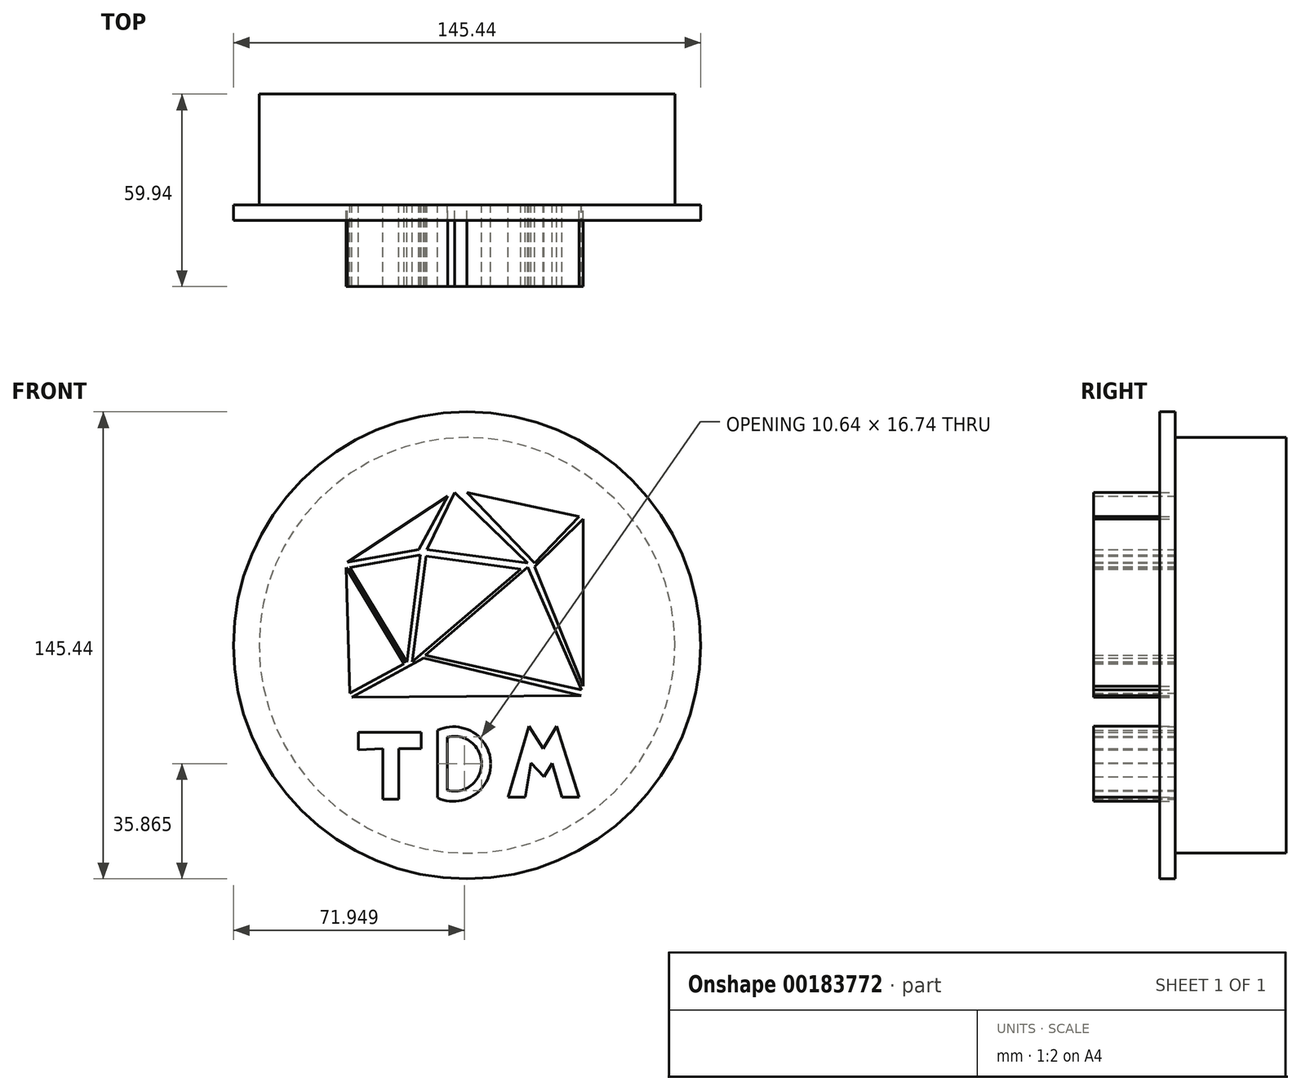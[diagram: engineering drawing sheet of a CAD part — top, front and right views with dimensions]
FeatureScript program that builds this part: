
annotation { "Feature Type Name" : "Feature", "Feature Type Description" : "" }
export const myFeature = defineFeature(function(context is Context, id is Id, definition is map)
    precondition{}
    {
        {
            var Q0;
            Q0=qCreatedBy(makeId("Front.planeOp"),FACE);
            var sketch = newSketch(context, id + "F0", { "sketchPlane" : qUnion([Q0])});
            skLineSegment(sketch, "E0", {"start": v(-26.25, -32.13) * mm, "end": v(-26.25, -47.88) * mm});
            skLineSegment(sketch, "E1", {"start": v(-26.25, -47.88) * mm, "end": v(-21.2, -47.88) * mm});
            skLineSegment(sketch, "E2", {"start": v(-21.2, -47.88) * mm, "end": v(-21.2, -32.13) * mm});
            skLineSegment(sketch, "E3", {"start": v(-21.2, -32.13) * mm, "end": v(-14.28, -32.13) * mm});
            skLineSegment(sketch, "E4", {"start": v(-14.28, -32.13) * mm, "end": v(-14.28, -27.09) * mm});
            skLineSegment(sketch, "E5", {"start": v(-14.28, -27.09) * mm, "end": v(-33.81, -27.09) * mm});
            skLineSegment(sketch, "E6", {"start": v(-33.81, -27.09) * mm, "end": v(-33.81, -32.55) * mm});
            skLineSegment(sketch, "E7", {"start": v(-33.81, -32.55) * mm, "end": v(-26.25, -32.13) * mm});
            skLineSegment(sketch, "E8", {"start": v(-9.24, -26.46) * mm, "end": v(-9.24, -47.46) * mm});
            skArc(sketch, "E9", {"start": v(-9.24, -47.46) * mm, "mid": v(7.38, -36.96) * mm, "end": v(-9.24, -26.46) * mm});
            skLineSegment(sketch, "E10", {"start": v(-6.1, -28.56) * mm, "end": v(-6.1, -45.15) * mm});
            skArc(sketch, "E11", {"start": v(-6.1, -45.15) * mm, "mid": v(4.55, -36.86) * mm, "end": v(-6.1, -28.56) * mm});
            skLineSegment(sketch, "E12", {"start": v(19.32, -25.2) * mm, "end": v(23.73, -32.13) * mm});
            skLineSegment(sketch, "E13", {"start": v(23.73, -32.13) * mm, "end": v(27.93, -25.2) * mm});
            skLineSegment(sketch, "E14", {"start": v(26.46, -36.75) * mm, "end": v(23.94, -40.95) * mm});
            skLineSegment(sketch, "E15", {"start": v(23.94, -40.95) * mm, "end": v(19.95, -36.54) * mm});
            skLineSegment(sketch, "E16", {"start": v(19.95, -36.54) * mm, "end": v(18.06, -47.25) * mm});
            skLineSegment(sketch, "E17", {"start": v(18.06, -47.25) * mm, "end": v(12.81, -47.25) * mm});
            skLineSegment(sketch, "E18", {"start": v(12.81, -47.25) * mm, "end": v(19.32, -25.2) * mm});
            skLineSegment(sketch, "E19", {"start": v(29.6, -47.25) * mm, "end": v(34.86, -47.25) * mm});
            skLineSegment(sketch, "E20", {"start": v(34.86, -47.25) * mm, "end": v(27.93, -25.2) * mm});
            skPoint(sketch, "E21.start.orphan", {"position": v(12.81, -46) * mm});
            skLineSegment(sketch, "E22", {"start": v(29.6, -47.25) * mm, "end": v(26.46, -36.75) * mm});
            skPoint(sketch, "E23.start.orphan", {"position": v(34.86, -45.15) * mm});
            skLineSegment(sketch, "E24", {"start": v(-37.2, 25.82) * mm, "end": v(-5.94, 46.51) * mm});
            skLineSegment(sketch, "E25", {"start": v(-5.94, 46.51) * mm, "end": v(-15.02, 29.84) * mm});
            skLineSegment(sketch, "E26", {"start": v(-15.02, 29.84) * mm, "end": v(-37.2, 25.82) * mm});
            skLineSegment(sketch, "E27", {"start": v(-12.5, 29.84) * mm, "end": v(-3.86, 47.56) * mm});
            skLineSegment(sketch, "E28", {"start": v(-3.86, 47.56) * mm, "end": v(18.92, 25.68) * mm});
            skLineSegment(sketch, "E29", {"start": v(18.92, 25.68) * mm, "end": v(-12.5, 29.84) * mm});
            skLineSegment(sketch, "E30", {"start": v(0, 47.56) * mm, "end": v(21, 25.68) * mm});
            skLineSegment(sketch, "E31", {"start": v(21, 25.68) * mm, "end": v(34.87, 40.1) * mm});
            skLineSegment(sketch, "E32", {"start": v(34.87, 40.1) * mm, "end": v(0, 47.56) * mm});
            skLineSegment(sketch, "E33", {"start": v(36.21, 39.34) * mm, "end": v(36.21, -12.73) * mm});
            skLineSegment(sketch, "E34", {"start": v(-36.49, 24.22) * mm, "end": v(-14.56, 28.2) * mm});
            skLineSegment(sketch, "E35", {"start": v(-14.56, 28.2) * mm, "end": v(-18.74, -5.28) * mm});
            skLineSegment(sketch, "E36", {"start": v(16.68, 23.74) * mm, "end": v(-12.79, 27.76) * mm});
            skLineSegment(sketch, "E37", {"start": v(34.25, -15.6) * mm, "end": v(-35.86, -16.15) * mm});
            skLineSegment(sketch, "E38", {"start": v(-35.86, -16.15) * mm, "end": v(-17.85, -6.35) * mm});
            skPoint(sketch, "E39.start.orphan", {"position": v(-17.85, -7.22) * mm});
            skLineSegment(sketch, "E40", {"start": v(-14.56, 28.2) * mm, "end": v(-36.49, 24.22) * mm});
            skLineSegment(sketch, "E41", {"start": v(-36.49, 24.22) * mm, "end": v(-18.74, -5.28) * mm});
            skPoint(sketch, "E42.orphan", {"position": v(-39.13, 23.74) * mm});
            skPoint(sketch, "E43.orphan", {"position": v(-41.22, 23.44) * mm});
            skPoint(sketch, "E44.start.orphan", {"position": v(20.1, 23.44) * mm});
            skPoint(sketch, "E45.start.orphan", {"position": v(34.25, -13.92) * mm});
            skLineSegment(sketch, "E46", {"start": v(-13.76, -5.65) * mm, "end": v(-13.55, -5.46) * mm});
            skLineSegment(sketch, "E47", {"start": v(-37.64, 24.22) * mm, "end": v(-19.64, -5.7) * mm});
            skLineSegment(sketch, "E48", {"start": v(-19.64, -5.7) * mm, "end": v(-36.49, -14.87) * mm});
            skLineSegment(sketch, "E49", {"start": v(-36.49, -14.87) * mm, "end": v(-37.64, 24.22) * mm});
            skLineSegment(sketch, "E50", {"start": v(-17, -5.14) * mm, "end": v(-12.79, 27.76) * mm});
            skLineSegment(sketch, "E51", {"start": v(-17, -5.14) * mm, "end": v(16.68, 23.74) * mm});
            skLineSegment(sketch, "E52", {"start": v(-13.04, -3.05) * mm, "end": v(18.92, 24.4) * mm});
            skLineSegment(sketch, "E53", {"start": v(18.92, 24.4) * mm, "end": v(35.69, -13.92) * mm});
            skLineSegment(sketch, "E54.trimOffspring", {"start": v(19.55, 22.96) * mm, "end": v(20.1, 23.44) * mm});
            skLineSegment(sketch, "E55", {"start": v(21, 24.46) * mm, "end": v(36.21, -12.73) * mm});
            skLineSegment(sketch, "E56", {"start": v(21, 24.46) * mm, "end": v(36.21, 39.34) * mm});
            skPoint(sketch, "E57.start.orphan", {"position": v(23.08, 25.68) * mm});
            skLineSegment(sketch, "E58", {"start": v(18.92, 24.4) * mm, "end": v(-13.04, -3.05) * mm});
            skLineSegment(sketch, "E59", {"start": v(-13.04, -3.05) * mm, "end": v(35.69, -13.92) * mm});
            skPoint(sketch, "E60.orphan", {"position": v(-15.47, -5.14) * mm});
            skLineSegment(sketch, "E61", {"start": v(-35.86, -16.15) * mm, "end": v(-13.55, -4) * mm});
            skLineSegment(sketch, "E62", {"start": v(35.56, -15.6) * mm, "end": v(-13.55, -4) * mm});
            skLineSegment(sketch, "E63", {"start": v(-35.86, -16.15) * mm, "end": v(35.56, -15.6) * mm});
            skSolve(sketch);
        }
        {
            var Q0;
            Q0 = qSketchRegion(id + "F0", true);
            extrude(context, id + "F1", {"entities" : qUnion([Q0]), "depth" : 25.4 * mm});
        }
        {
            var Q0;
            Q0=qCreatedBy(makeId("Front.planeOp"),FACE);
            var sketch = newSketch(context, id + "F2", { "sketchPlane" : qUnion([Q0])});
            skCircle(sketch, "E64", {"center": v(0, 0) * mm, "radius": 71.55 * mm});
            skCircle(sketch, "E65", {"center": v(0, 0) * mm, "radius": 64.71 * mm});
            skSolve(sketch);
        }
        {
            var Q0;
            Q0=makeQuery(id+"F2.imprint","IMPRINT",FACE,{"disambiguationData":[TD([[makeQuery(id+"F2.imprint","IMPRINT",EDGE,{"derivedFrom":sQuery(id+"F2.wireOp",EDGE,"E65")}),1.0]])]});
            extrude(context, id + "F3", {"entities" : qUnion([Q0]), "oppositeDirection" : true, "depth" : 34.54 * mm});
        }
        {
            var Q0;
            Q0=qCreatedBy(makeId("Front.planeOp"),FACE);
            var sketch = newSketch(context, id + "F4", { "sketchPlane" : qUnion([Q0])});
            skCircle(sketch, "E66", {"center": v(0, 0) * mm, "radius": 72.72 * mm});
            skSolve(sketch);
        }
        {
            var Q0;
            Q0=makeQuery(id+"F4.imprint","IMPRINT",FACE,{"disambiguationData":[TD([[makeQuery(id+"F4.imprint","IMPRINT",EDGE,{"derivedFrom":sQuery(id+"F4.wireOp",EDGE,"E66")}),1.0]])]});
            extrude(context, id + "F5", {"entities" : qUnion([Q0]), "depth" : 4.83 * mm});
        }
    });
